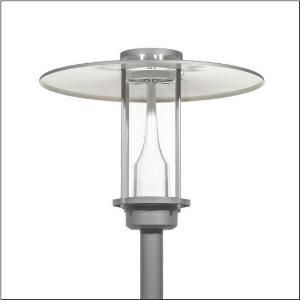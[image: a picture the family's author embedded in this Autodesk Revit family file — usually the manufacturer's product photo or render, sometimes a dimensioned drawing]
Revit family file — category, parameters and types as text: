
# Revit family: city-light_plus_iq___p1_0a_5xa5275ff14hp_3a67
name_source: partatom
category: Lighting Fixtures
units: mm (PartAtom-declared; Revit-internal decimal feet)

## family parameters
Cut with Voids When Loaded = No
Host = Face
Light Source = No
Part Type = Normal
Room Calculation Point = No
Round Connector Dimension = Use Diameter
Shared = No

## types (1)
- --- (1 x LED, 4480 lm, 33.6 W, 3000K)
    Apparent Load = 34 VA
    CIE Flux Codes = 30 60 90 96 100
    Color Rendering = 70
    Color Temperature = 3000K
    Default Elevation = 1800 mm
    Description = City-Light Plus iQ, mast luminaire, Module 540 iQ-SR, primary light control with 3 zone facetted reflector, of plastic, silver coated, highly specular, structured, primary optical cover: cover, of PMMA, transparent, light distribution: P1.0a, light emission: direct distribution, primary light characteristic: strongly asymmetric, installation type: post-top, LED, High Power LED, rated luminous flux: 4.480lm, luminous efficacy: 133lm/W, light colour: 730, colour temperature: 3000K, control gear: ECG iQ, control: presetting dimming logarithmic, Street-Remote, Auto-Match, Temp-Guard, Lumen-Switch, Night-Set, Smart-Wire, Light-Fading, Desk-Remote (wireless, voltage-free reading and setting of iQ features in the workshop via application-optimized NFC function/RFID function), optimised constant luminous flux control (CLO 2.0), with terminal, 6-pole, max. 2.5mm², mains connection: 230..240V, AC, 50/60Hz, start of lifetime: 34W, end of service life: 36W, reduction: 15W, luminaire housing, upper part, of glass-fibre reinforced polyester, coated, Siteco® metallic grey (DB 702S), diameter: 750mm, height: 590mm, spigot size: d x l = 76 x 70mm (post-top) | with reducer (optional accessory) 60 x 70mm, post-top mast mounting element, of diecast aluminium, coated, Siteco® metallic grey (DB 702S), Module 540 iQ-SR, traffic white (RAL 9016), equipment: Power, protection rating (complete): IP65, insulation class (complete): insulation class II (safety insulation), certification: CE, ENEC, VDE, packaging unit: 1 piece

Light Distribution: P1.0a
    Height = 590 mm
    Lamp = 1 x LED
    Lamp Light Flux = 4480 lm
    Lamp Power = 33.6 W
    Lamp count = 1
    Length = 750 mm
    Luminous efficacy = 133 lm/W
    Manufacturer = Siteco
    ModVariant = No
    Model = 5XA5275FF14HP
    Number of Poles = 1
    OnlyDefault = Yes
    Power Factor = 1
    Product Name = City-Light Plus iQ | P1.0a
    Product group = mast luminaire | pylon top
    ProductGroupID = 6100
    Protection Class = Protection class II
    Protection Degree = IP 65
    RLX_Detail_Level = 1
    RLX_Emergency_Light_Flux = 0 lm
    RLX_Emergency_Type = 0
    RLX_Emergency_Type_DB = No
    RlxData = <blob elided: 52589 chars, md5=7676bd57>
    Socket = socket
    Standby Power = 0 W
    System Light Flux = 4480 lm
    System Power = 34 W
    Type Comments = factory setting: luminous flux: 100 % | dim-lin: 254 | 695 mA
    Type Image = l_1006456.jpg
    URL = http://relux.com
    VarID = @adj_146379
    Voltage = 0 V
    Weight = 0.00 kg
    Width = 0 mm  [stored 0 ft]

note: [stored X ft] marks values corroborated as IEEE doubles in the binary element streams (Revit-internal decimal feet)

## geometry (parser evidence)
native form markers: Blend x4, Sweep x10
no freeform markers — native parametric forms only
